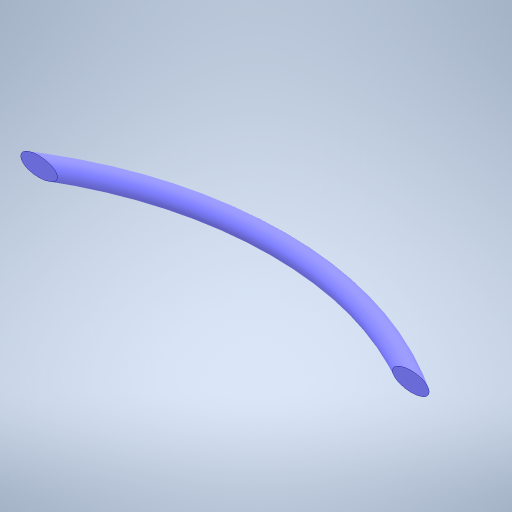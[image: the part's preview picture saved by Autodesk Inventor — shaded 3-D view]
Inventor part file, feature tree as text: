
AUTODESK INVENTOR PART (.ipt)
format: ipt  version: 2024 (Build 280153000, 153)  size: 267,264 bytes
history: native  units: in
note: dims shown in document units (in); Inventor stores cm internally (conversion verified against a paired STEP export)
features: sketch x2, revolve x1, extrude x1
ambient origin geometry x8: Origin, YZ Plane, XZ Plane, XY Plane, X Axis, Y Axis, Z Axis, Center Point
bodies: Solid1 (feature_tree)
feature tree (4):
  revolve  "Revolution1"  [1 undecoded]
  extrude  "Extrusion1"  Depth=16.0in
  sketch  "Sketch1"  dims[d0=0.75in d1=14.0in]
  sketch  "Sketch2"  dims[d2=90.0deg d3=16.0in d4=1.0in d5=0.0in]
note: 1 required parameter value undecoded (feature->parameter linkage not recoverable at this tier; creation-order binding heuristic only, values carry confidence <= 0.55)
